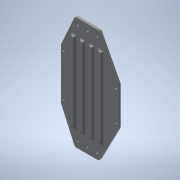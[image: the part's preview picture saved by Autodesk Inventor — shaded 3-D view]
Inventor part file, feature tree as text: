
AUTODESK INVENTOR PART (.ipt)
format: ipt  version: 2020 (Build 240168000, 168)  size: 640,000 bytes
history: native  units: mm
features: sketch x17, extrude x13, projected_geometry x12, fillet x6, hole x5, chamfer x3, plane x1, mirror x1, pattern_linear x1
ambient origin geometry x8: Origin, YZ Plane, XZ Plane, XY Plane, X Axis, Y Axis, Z Axis, Center Point
bodies: Solid1 (feature_tree)
feature tree (59):
  extrude  "Extrusion1"  Depth=76.0mm
  hole  "Hole1"  [1 undecoded]
  extrude  "Extrusion2"  Depth=40.0mm
  extrude  "Extrusion5"  Depth=2.0mm
  extrude  "Extrusion3"  Depth=3.0mm TaperAngle=0.0deg
  extrude  "Extrusion4"  Depth=3.0mm TaperAngle=0.0deg
  sketch  "Sketch8"  dims[d18=43.0mm d20=3.0mm d21=0.0mm]
  hole  "Hole2"  [1 undecoded]
  hole  "Hole3"  [1 undecoded]
  extrude  "Extrusion6"  Depth=17.0624mm
  extrude  "Extrusion7"  Depth=2.0mm
  extrude  "Extrusion10"  Depth=3.0mm TaperAngle=0.0deg
  chamfer  "Chamfer3"  Distance=4.957359mm
  plane  "Work Plane1"
  extrude  "Extrusion11"  Depth=2.0mm TaperAngle=0.0deg
  fillet  "Fillet1"  Radius=4.957359mm
  extrude  "Extrusion12"  TaperAngle=0.0deg  [1 undecoded]
  chamfer  "Chamfer4"  Distance=11.2mm
  chamfer  "Chamfer5"  Distance=10.0mm Angle=45.0deg
  fillet  "Fillet2"  [1 undecoded]
  fillet  "Fillet3"  Radius=8.0mm
  extrude  "Extrusion13"  Depth=2.0mm
  fillet  "Fillet4"  Radius=9.5mm
  hole  "Hole4"  [1 undecoded]
  mirror  "Mirror2"
  extrude  "Extrusion14"  Depth=2.0mm TaperAngle=0.0deg
  hole  "Hole5"  [1 undecoded]
  fillet  "Fillet5"  Radius=18.0mm
  extrude  "Extrusion15"  Depth=2.0mm TaperAngle=0.0deg
  fillet  "Fillet6"  Radius=10.0mm
  pattern_linear  "Rectangular Pattern1"  Spacing1=4.24mm  [1 undecoded]
  sketch  "Sketch1"  dims[d0=76.0mm d1=143.6mm]
  sketch  "Sketch2"  dims[d2=3.0mm d3=0.0mm d4=8.0mm]
  sketch  "Sketch4"  dims[d5=70.0mm d6=40.0mm]
  sketch  "Sketch5"  dims[d7=3.2mm d8=6.0mm d9=6.3mm d10=2.0mm d11=90.0deg d12=8.0mm d13=20.594885mm d14=38.0mm]
  projected_geometry  "Projected Loop1"
  sketch  "Sketch7"  dims[d15=17.0mm d16=3.0mm d17=0.0mm]
  projected_geometry  "Projected Loop3"
  projected_geometry  "Projected Loop4"
  sketch  "Sketch10"  dims[d22=25.4mm d23=3.0mm d24=0.0mm]
  projected_geometry  "Projected Loop5"
  sketch  "Sketch11"  dims[d25=14.0mm d26=12.7mm]
  projected_geometry  "Projected Loop6"
  sketch  "Sketch12"  dims[d27=17.4625mm d30=17.0624mm]
  projected_geometry  "Projected Loop7"
  sketch  "Sketch16"  dims[d31=5.0mm]
  projected_geometry  "Projected Loop11"
  projected_geometry  "Projected Loop12"
  sketch  "Sketch17"  dims[d32=4.3mm d33=6.0mm d34=9.4mm d35=2.0mm d36=90.0deg d37=8.0mm d38=20.594885mm]
  projected_geometry  "Projected Loop13"
  sketch  "Sketch18"  dims[d39=5.3mm d40=6.0mm d41=10.4mm d42=2.0mm d43=90.0deg d44=8.0mm d45=20.594885mm d46=46.0mm]
  projected_geometry  "Projected Loop14"
  sketch  "Sketch19"  dims[d47=24.0mm d48=3.0mm d49=0.0mm]
  sketch  "Sketch20"  dims[d50=135.0deg]
  sketch  "Sketch21"  dims[d51=135.0deg]
  sketch  "Sketch22"  dims[d52=7.0mm]
  projected_geometry  "Projected Loop15"
  sketch  "Sketch23"  dims[d53=6.0mm d54=4.957359mm d55=50.0mm d56=0.0mm d57=4.957359mm d58=0.0mm d59=0.0mm d71=11.2mm d72=0.0mm d73=11.2mm d74=10.0mm d75=45.0deg d76=-18.0mm d77=8.0mm d78=8.0mm d79=9.5mm d80=9.5mm d81=15.0mm d82=0.0mm d83=2.0mm d84=18.0mm d85=15.0mm d86=0.0mm d87=15.0mm d88=10.0mm d89=45.0deg d90=4.24mm d91=10.0mm d92=45.0deg d93=1.0mm d94=3.0mm d95=15.0mm d96=0.0mm d97=1.0mm d98=26.0mm d99=10.0mm d100=12.0mm d101=2.459mm d102=6.0mm d103=10.4mm d104=2.0mm d105=90.0deg d106=10.0mm d107=20.594885mm d108=15.0mm d109=0.0mm d110=3.2mm d111=6.0mm d112=6.3mm d113=2.0mm d114=90.0deg d115=10.0mm d116=20.594885mm d117=3.0mm d118=4.0mm d119=105.0mm d120=15.0mm d121=2.0mm d122=0.0mm d123=2.0mm d124=40.0mm d126=12.0mm]
  projected_geometry  "Projected Loop16"
note: 8 required parameter values undecoded (feature->parameter linkage not recoverable at this tier; creation-order binding heuristic only, values carry confidence <= 0.55)
